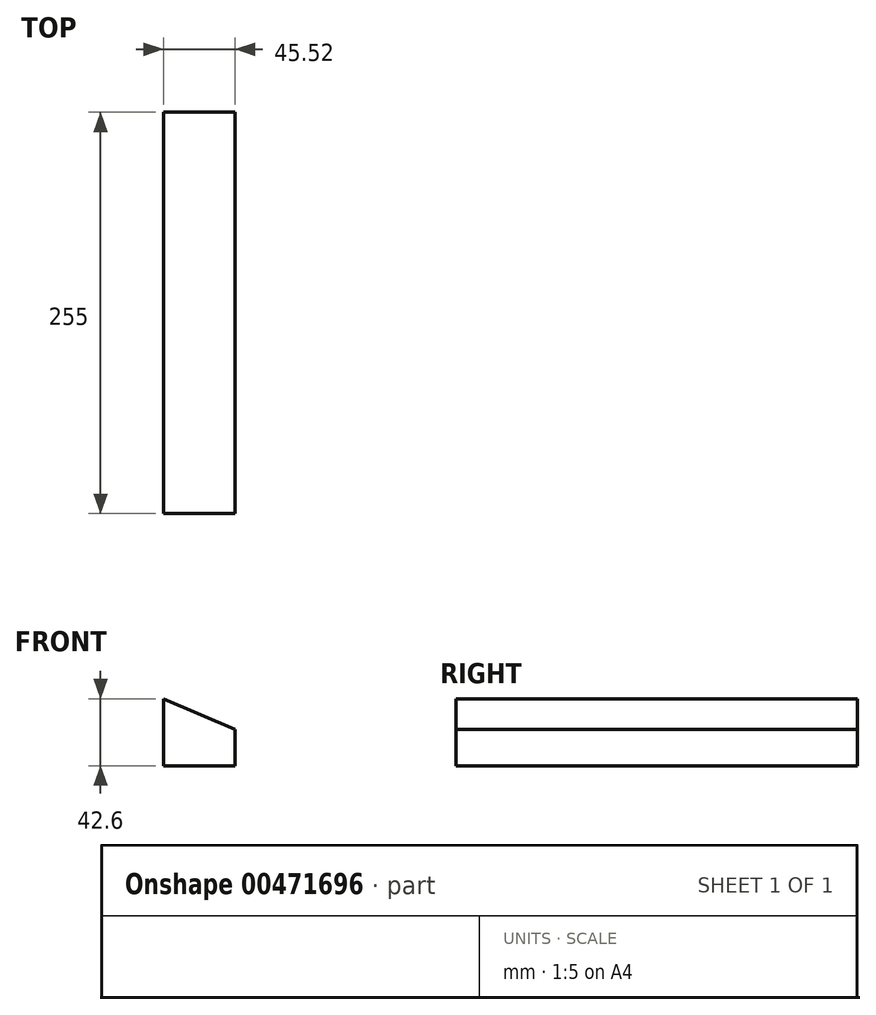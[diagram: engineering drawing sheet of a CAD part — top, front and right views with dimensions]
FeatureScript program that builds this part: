
annotation { "Feature Type Name" : "Feature", "Feature Type Description" : "" }
export const myFeature = defineFeature(function(context is Context, id is Id, definition is map)
    precondition{}
    {
        {
            var Q0;
            Q0=qCreatedBy(makeId("Front.planeOp"),FACE);
            var sketch = newSketch(context, id + "F0", { "sketchPlane" : qUnion([Q0])});
            skLineSegment(sketch, "E0.bottom", {"start": v(-22.97, 0) * mm, "end": v(22.55, 0) * mm});
            skLineSegment(sketch, "E0.left", {"start": v(-22.97, 0) * mm, "end": v(-22.97, 42.6) * mm});
            skLineSegment(sketch, "E0.right", {"start": v(22.55, 0) * mm, "end": v(22.55, 23) * mm});
            skLineSegment(sketch, "E1", {"start": v(-22.97, 42.6) * mm, "end": v(22.55, 23) * mm});
            skSolve(sketch);
        }
        {
            var Q0;
            Q0 = qSketchRegion(id + "F0", true);
            extrude(context, id + "F1", {"entities" : qUnion([Q0]), "depth" : 255 * mm});
        }
    });
